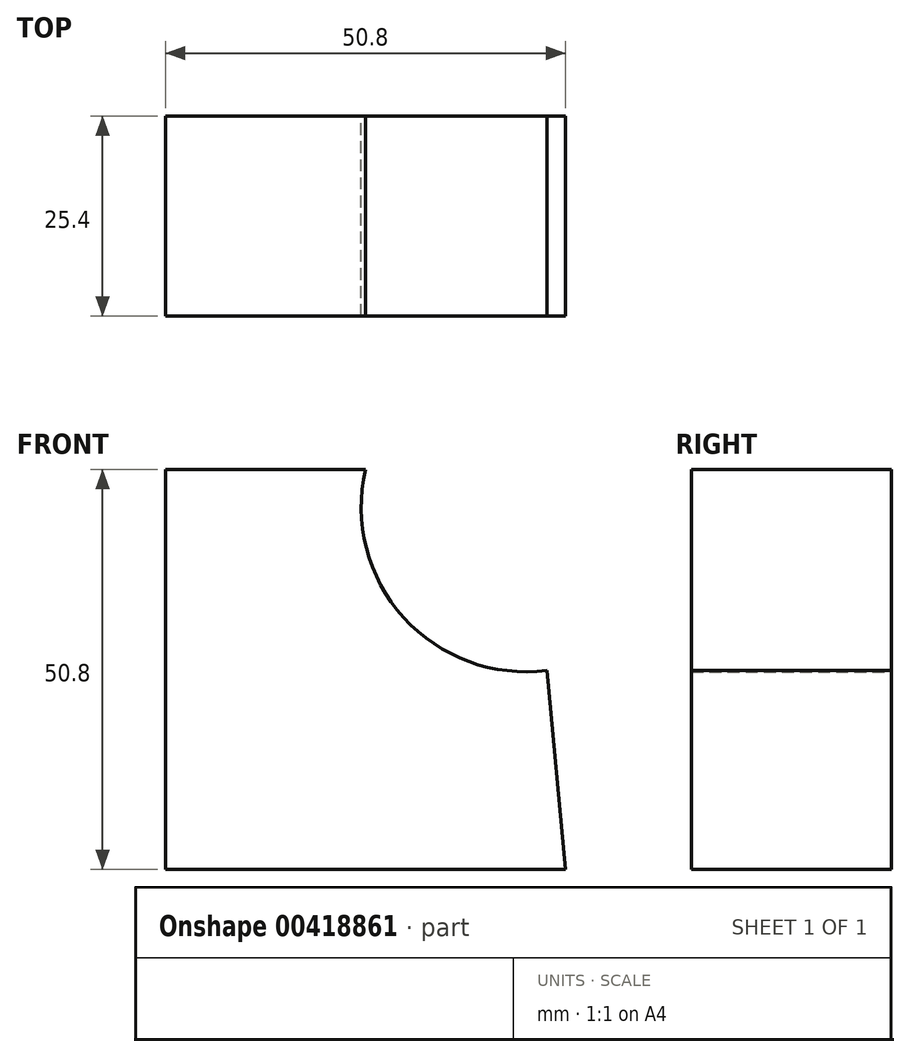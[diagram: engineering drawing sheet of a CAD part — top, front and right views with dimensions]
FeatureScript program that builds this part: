
annotation { "Feature Type Name" : "Feature", "Feature Type Description" : "" }
export const myFeature = defineFeature(function(context is Context, id is Id, definition is map)
    precondition{}
    {
        {
            var Q0;
            Q0=qCreatedBy(makeId("Front.planeOp"),FACE);
            var sketch = newSketch(context, id + "F0", { "sketchPlane" : qUnion([Q0])});
            skLineSegment(sketch, "E0", {"start": v(0, 0) * mm, "end": v(-50.8, 0) * mm});
            skLineSegment(sketch, "E1", {"start": v(-50.8, 0) * mm, "end": v(-50.8, 50.8) * mm});
            skLineSegment(sketch, "E2", {"start": v(-50.8, 50.8) * mm, "end": v(-25.4, 50.8) * mm});
            skLineSegment(sketch, "E3", {"start": v(0, 0) * mm, "end": v(-2.33, 25.3) * mm});
            skArc(sketch, "E4", {"start": v(-25.4, 50.8) * mm, "mid": v(-20.55, 32) * mm, "end": v(-2.33, 25.3) * mm});
            skSolve(sketch);
        }
        {
            var Q0;
            Q0=makeQuery(id+"F0.imprint","IMPRINT",FACE,{"disambiguationData":[TD([[makeQuery(id+"F0.imprint","IMPRINT",EDGE,{"derivedFrom":sQuery(id+"F0.wireOp",EDGE,"E0")}),-1.0]])]});
            extrude(context, id + "F1", {"entities" : qUnion([Q0]), "depth" : 25.4 * mm});
        }
    });
